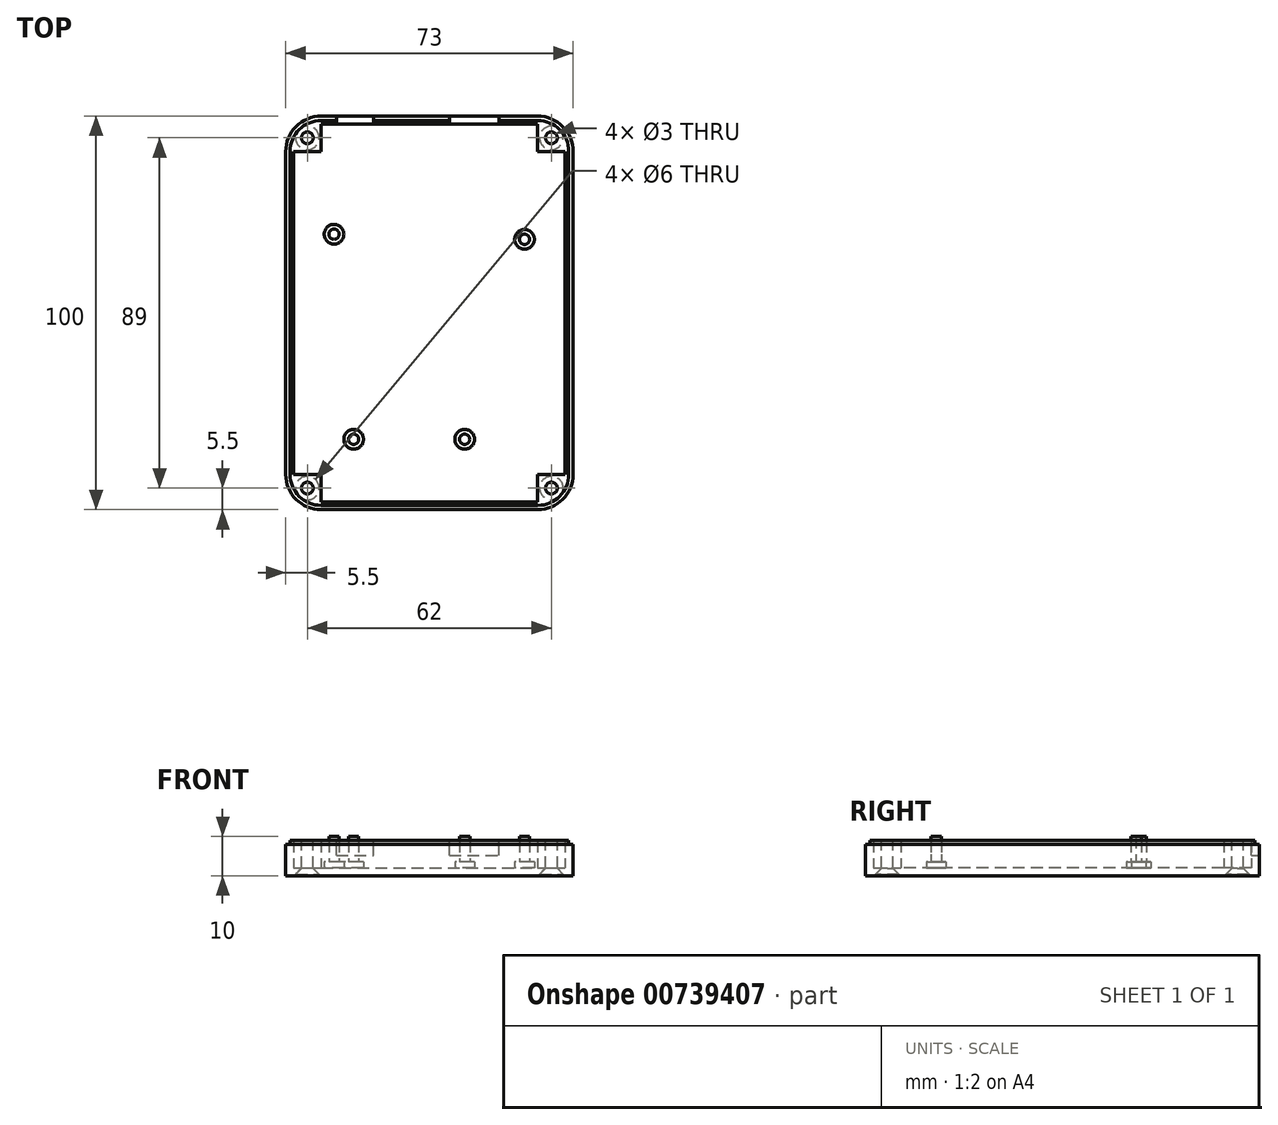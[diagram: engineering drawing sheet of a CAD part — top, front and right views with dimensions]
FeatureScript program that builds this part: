
annotation { "Feature Type Name" : "Feature", "Feature Type Description" : "" }
export const myFeature = defineFeature(function(context is Context, id is Id, definition is map)
    precondition{}
    {
        {
            var Q0;
            Q0=qCreatedBy(makeId("Top.planeOp"),FACE);
            var sketch = newSketch(context, id + "F0", { "sketchPlane" : qUnion([Q0])});
            skLineSegment(sketch, "E0.bottom", {"start": v(-27.5, 63.5) * mm, "end": v(27.5, 63.5) * mm});
            skLineSegment(sketch, "E0.top", {"start": v(-27.5, -36.5) * mm, "end": v(27.5, -36.5) * mm});
            skLineSegment(sketch, "E0.left", {"start": v(-36.5, 54.5) * mm, "end": v(-36.5, -27.5) * mm});
            skLineSegment(sketch, "E0.right", {"start": v(36.5, 54.5) * mm, "end": v(36.5, -27.5) * mm});
            skPoint(sketch, "E1.visualSharp", {"position": v(-36.5, 63.5) * mm});
            skArc(sketch, "E1.filletArc", {"start": v(-27.5, 63.5) * mm, "mid": v(-33.86, 60.86) * mm, "end": v(-36.5, 54.5) * mm});
            skPoint(sketch, "E2.visualSharp", {"position": v(36.5, 63.5) * mm});
            skArc(sketch, "E2.filletArc", {"start": v(36.5, 54.5) * mm, "mid": v(33.86, 60.86) * mm, "end": v(27.5, 63.5) * mm});
            skPoint(sketch, "E3.visualSharp", {"position": v(36.5, -36.5) * mm});
            skArc(sketch, "E3.filletArc", {"start": v(27.5, -36.5) * mm, "mid": v(33.86, -33.86) * mm, "end": v(36.5, -27.5) * mm});
            skPoint(sketch, "E4.visualSharp", {"position": v(-36.5, -36.5) * mm});
            skArc(sketch, "E4.filletArc", {"start": v(-36.5, -27.5) * mm, "mid": v(-33.86, -33.86) * mm, "end": v(-27.5, -36.5) * mm});
            skSolve(sketch);
        }
        {
            var Q0;
            Q0=qSketchRegion(id+"F0",true);
            extrude(context, id + "F1", {"entities" : qUnion([Q0]), "depth" : 2 * mm});
        }
        {
            var Q0;
            Q0=makeQuery(id+"F1.opExtrude","CAP_FACE",FACE,{"disambiguationData":[OSD([sQuery(id+"F0.wireOp",EDGE,"E0.bottom"),sQuery(id+"F0.wireOp",EDGE,"E0.top"),sQuery(id+"F0.wireOp",EDGE,"E0.left"),sQuery(id+"F0.wireOp",EDGE,"E0.right")])],"isStart":false});
            var sketch = newSketch(context, id + "F2", { "sketchPlane" : qUnion([Q0])});
            skCircle(sketch, "E5", {"center": v(-19.24, -18.6) * mm, "radius": 2.5 * mm});
            skCircle(sketch, "E6", {"center": v(8.96, -18.6) * mm, "radius": 2.5 * mm});
            skCircle(sketch, "E7", {"center": v(24.16, 32.2) * mm, "radius": 2.5 * mm});
            skCircle(sketch, "E8", {"center": v(-24.24, 33.5) * mm, "radius": 2.5 * mm});
            skSolve(sketch);
        }
        {
            var Q0;
            Q0=qSketchRegion(id+"F2",true);
            extrude(context, id + "F3", {"entities" : qUnion([Q0]), "operationType" : NewBodyOperationType.ADD, "depth" : 1.5 * mm});
        }
        {
            var Q0;
            Q0=makeQuery(id+"F3.opExtrude","CAP_FACE",FACE,{"disambiguationData":[OSD([sQuery(id+"F2.wireOp",EDGE,"E8")])],"isStart":false});
            var sketch = newSketch(context, id + "F4", { "sketchPlane" : qUnion([Q0])});
            skCircle(sketch, "E9", {"center": v(-19.24, -18.6) * mm, "radius": 1.3 * mm});
            skCircle(sketch, "E10", {"center": v(8.96, -18.6) * mm, "radius": 1.3 * mm});
            skCircle(sketch, "E11", {"center": v(24.16, 32.2) * mm, "radius": 1.3 * mm});
            skCircle(sketch, "E12", {"center": v(-24.24, 33.5) * mm, "radius": 1.3 * mm});
            skSolve(sketch);
        }
        {
            var Q0;
            Q0=qSketchRegion(id+"F4",true);
            extrude(context, id + "F5", {"entities" : qUnion([Q0]), "operationType" : NewBodyOperationType.ADD, "depth" : 1.5 * mm});
        }
        {
            var Q0;
            Q0=makeQuery(id+"F1.opExtrude","CAP_FACE",FACE,{"disambiguationData":[OSD([sQuery(id+"F0.wireOp",EDGE,"E0.bottom"),sQuery(id+"F0.wireOp",EDGE,"E0.top"),sQuery(id+"F0.wireOp",EDGE,"E0.left"),sQuery(id+"F0.wireOp",EDGE,"E0.right"),sQuery(id+"F0.wireOp",EDGE,"E1.filletArc"),sQuery(id+"F0.wireOp",EDGE,"E2.filletArc"),sQuery(id+"F0.wireOp",EDGE,"E3.filletArc"),sQuery(id+"F0.wireOp",EDGE,"E4.filletArc")])],"isStart":false});
            var sketch = newSketch(context, id + "F6", { "sketchPlane" : qUnion([Q0])});
            skLineSegment(sketch, "E13.bottom", {"start": v(-27.5, 63.5) * mm, "end": v(27.5, 63.5) * mm});
            skLineSegment(sketch, "E13.top", {"start": v(-27.5, -36.5) * mm, "end": v(27.5, -36.5) * mm});
            skLineSegment(sketch, "E13.left", {"start": v(-36.5, 54.5) * mm, "end": v(-36.5, -27.5) * mm});
            skLineSegment(sketch, "E13.right", {"start": v(36.5, 54.5) * mm, "end": v(36.5, -27.5) * mm});
            skPoint(sketch, "E14.visualSharp", {"position": v(-36.5, 63.5) * mm});
            skArc(sketch, "E14.filletArc", {"start": v(-27.5, 63.5) * mm, "mid": v(-33.86, 60.86) * mm, "end": v(-36.5, 54.5) * mm});
            skPoint(sketch, "E15.visualSharp", {"position": v(36.5, 63.5) * mm});
            skArc(sketch, "E15.filletArc", {"start": v(36.5, 54.5) * mm, "mid": v(33.86, 60.86) * mm, "end": v(27.5, 63.5) * mm});
            skPoint(sketch, "E16.visualSharp", {"position": v(36.5, -36.5) * mm});
            skArc(sketch, "E16.filletArc", {"start": v(27.5, -36.5) * mm, "mid": v(33.86, -33.86) * mm, "end": v(36.5, -27.5) * mm});
            skPoint(sketch, "E17.visualSharp", {"position": v(-36.5, -36.5) * mm});
            skArc(sketch, "E17.filletArc", {"start": v(-36.5, -27.5) * mm, "mid": v(-33.86, -33.86) * mm, "end": v(-27.5, -36.5) * mm});
            skLineSegment(sketch, "E18", {"start": v(-27.5, 61.5) * mm, "end": v(27.5, 61.5) * mm});
            skLineSegment(sketch, "E19", {"start": v(-34.5, 54.5) * mm, "end": v(-34.5, -27.5) * mm});
            skLineSegment(sketch, "E20", {"start": v(-27.5, -34.5) * mm, "end": v(27.5, -34.5) * mm});
            skLineSegment(sketch, "E21", {"start": v(34.5, 54.5) * mm, "end": v(34.5, -27.5) * mm});
            skLineSegment(sketch, "E22", {"start": v(-34.5, 54.5) * mm, "end": v(-27.5, 54.5) * mm});
            skLineSegment(sketch, "E23", {"start": v(-27.5, 61.5) * mm, "end": v(-27.5, 54.5) * mm});
            skLineSegment(sketch, "E24", {"start": v(27.5, 61.5) * mm, "end": v(27.5, 54.5) * mm});
            skLineSegment(sketch, "E25", {"start": v(27.5, 54.5) * mm, "end": v(34.5, 54.5) * mm});
            skLineSegment(sketch, "E26", {"start": v(-34.5, -27.5) * mm, "end": v(-27.5, -27.5) * mm});
            skLineSegment(sketch, "E27", {"start": v(-27.5, -34.5) * mm, "end": v(-27.5, -27.5) * mm});
            skLineSegment(sketch, "E28", {"start": v(27.5, -34.5) * mm, "end": v(27.5, -27.5) * mm});
            skLineSegment(sketch, "E29", {"start": v(27.5, -27.5) * mm, "end": v(34.5, -27.5) * mm});
            skSolve(sketch);
        }
        {
            var Q0;
            Q0=qSketchRegion(id+"F6",true);
            extrude(context, id + "F7", {"entities" : qUnion([Q0]), "operationType" : NewBodyOperationType.ADD, "depth" : 7 * mm});
        }
        {
            var Q0;
            Q0=makeQuery(id+"F7.opExtrude","CAP_FACE",FACE,{"disambiguationData":[OSD([sQuery(id+"F6.wireOp",EDGE,"E13.bottom"),sQuery(id+"F6.wireOp",EDGE,"E13.top"),sQuery(id+"F6.wireOp",EDGE,"E13.left"),sQuery(id+"F6.wireOp",EDGE,"E13.right"),sQuery(id+"F6.wireOp",EDGE,"E14.filletArc"),sQuery(id+"F6.wireOp",EDGE,"E15.filletArc"),sQuery(id+"F6.wireOp",EDGE,"E16.filletArc"),sQuery(id+"F6.wireOp",EDGE,"E17.filletArc"),sQuery(id+"F6.wireOp",EDGE,"E18"),sQuery(id+"F6.wireOp",EDGE,"E19"),sQuery(id+"F6.wireOp",EDGE,"E20"),sQuery(id+"F6.wireOp",EDGE,"E21"),sQuery(id+"F6.wireOp",EDGE,"E22"),sQuery(id+"F6.wireOp",EDGE,"E23"),sQuery(id+"F6.wireOp",EDGE,"E24"),sQuery(id+"F6.wireOp",EDGE,"E25"),sQuery(id+"F6.wireOp",EDGE,"E26"),sQuery(id+"F6.wireOp",EDGE,"E27"),sQuery(id+"F6.wireOp",EDGE,"E28"),sQuery(id+"F6.wireOp",EDGE,"E29")])],"isStart":false});
            var sketch = newSketch(context, id + "F8", { "sketchPlane" : qUnion([Q0])});
            skCircle(sketch, "E30", {"center": v(-31, 58) * mm, "radius": 1.5 * mm});
            skCircle(sketch, "E31", {"center": v(31, 58) * mm, "radius": 1.5 * mm});
            skCircle(sketch, "E32", {"center": v(-31, -31) * mm, "radius": 1.5 * mm});
            skCircle(sketch, "E33", {"center": v(31, -31) * mm, "radius": 1.5 * mm});
            skSolve(sketch);
        }
        {
            var Q0;
            Q0=qSketchRegion(id+"F8",true);
            extrude(context, id + "F9", {"entities" : qUnion([Q0]), "operationType" : NewBodyOperationType.REMOVE, "oppositeDirection" : true, "depth" : 10 * mm});
        }
        {
            var Q0;
            Q0=makeQuery(id+"F7.opExtrude","CAP_FACE",FACE,{"disambiguationData":[OSD([sQuery(id+"F6.wireOp",EDGE,"E13.bottom"),sQuery(id+"F6.wireOp",EDGE,"E13.top"),sQuery(id+"F6.wireOp",EDGE,"E13.left"),sQuery(id+"F6.wireOp",EDGE,"E13.right"),sQuery(id+"F6.wireOp",EDGE,"E14.filletArc"),sQuery(id+"F6.wireOp",EDGE,"E15.filletArc"),sQuery(id+"F6.wireOp",EDGE,"E16.filletArc"),sQuery(id+"F6.wireOp",EDGE,"E17.filletArc"),sQuery(id+"F6.wireOp",EDGE,"E18"),sQuery(id+"F6.wireOp",EDGE,"E19"),sQuery(id+"F6.wireOp",EDGE,"E20"),sQuery(id+"F6.wireOp",EDGE,"E21"),sQuery(id+"F6.wireOp",EDGE,"E22"),sQuery(id+"F6.wireOp",EDGE,"E23"),sQuery(id+"F6.wireOp",EDGE,"E24"),sQuery(id+"F6.wireOp",EDGE,"E25"),sQuery(id+"F6.wireOp",EDGE,"E26"),sQuery(id+"F6.wireOp",EDGE,"E27"),sQuery(id+"F6.wireOp",EDGE,"E28"),sQuery(id+"F6.wireOp",EDGE,"E29")])],"isStart":false});
            var sketch = newSketch(context, id + "F10", { "sketchPlane" : qUnion([Q0])});
            skLineSegment(sketch, "E34.bottom", {"start": v(17.66, 61.5) * mm, "end": v(5.06, 61.5) * mm});
            skLineSegment(sketch, "E34.top", {"start": v(17.66, 63.5) * mm, "end": v(5.06, 63.5) * mm});
            skLineSegment(sketch, "E34.left", {"start": v(17.66, 61.5) * mm, "end": v(17.66, 63.5) * mm});
            skLineSegment(sketch, "E34.right", {"start": v(5.06, 61.5) * mm, "end": v(5.06, 63.5) * mm});
            skLineSegment(sketch, "E35.bottom", {"start": v(-14.14, 61.5) * mm, "end": v(-23.64, 61.5) * mm});
            skLineSegment(sketch, "E35.top", {"start": v(-14.14, 63.5) * mm, "end": v(-23.64, 63.5) * mm});
            skLineSegment(sketch, "E35.left", {"start": v(-14.14, 61.5) * mm, "end": v(-14.14, 63.5) * mm});
            skLineSegment(sketch, "E35.right", {"start": v(-23.64, 61.5) * mm, "end": v(-23.64, 63.5) * mm});
            skSolve(sketch);
        }
        {
            var Q0;
            Q0=qSketchRegion(id+"F10",true);
            extrude(context, id + "F11", {"entities" : qUnion([Q0]), "operationType" : NewBodyOperationType.REMOVE, "oppositeDirection" : true, "depth" : 3.8 * mm});
        }
        {
            var Q0;
            Q0=makeQuery(id+"F1.opExtrude","CAP_FACE",FACE,{"disambiguationData":[OSD([sQuery(id+"F0.wireOp",EDGE,"E0.bottom"),sQuery(id+"F0.wireOp",EDGE,"E0.top"),sQuery(id+"F0.wireOp",EDGE,"E0.left"),sQuery(id+"F0.wireOp",EDGE,"E0.right"),sQuery(id+"F0.wireOp",EDGE,"E1.filletArc"),sQuery(id+"F0.wireOp",EDGE,"E2.filletArc"),sQuery(id+"F0.wireOp",EDGE,"E3.filletArc"),sQuery(id+"F0.wireOp",EDGE,"E4.filletArc")])],"isStart":true});
            var sketch = newSketch(context, id + "F12", { "sketchPlane" : qUnion([Q0])});
            skCircle(sketch, "E36", {"center": v(31, -58) * mm, "radius": 3 * mm});
            skCircle(sketch, "E37", {"center": v(-31, -58) * mm, "radius": 3 * mm});
            skCircle(sketch, "E38", {"center": v(-31, 31) * mm, "radius": 3 * mm});
            skCircle(sketch, "E39", {"center": v(31, 31) * mm, "radius": 3 * mm});
            skSolve(sketch);
        }
        {
            var Q0;
            Q0=qSketchRegion(id+"F12",true);
            extrude(context, id + "F13", {"entities" : qUnion([Q0]), "operationType" : NewBodyOperationType.REMOVE, "oppositeDirection" : true, "depth" : .4 * mm});
        }
        {
            var Q0;
            Q0=makeQuery(id+"F13.boolean.opBoolean","INTERSECT",EDGE,{"derivedFrom":[makeQuery(id+"F9.boolean.opBoolean","COPY",FACE,{"derivedFrom":makeQuery(id+"F9.opExtrude","SWEPT_FACE",FACE,{"disambiguationData":[OSD([sQuery(id+"F8.wireOp",EDGE,"E31")])]})}),makeQuery(id+"F13.opExtrude","CAP_FACE",FACE,{"disambiguationData":[OSD([sQuery(id+"F12.wireOp",EDGE,"E36")])],"isStart":false})]});
            var Q1;
            Q1=makeQuery(id+"F13.boolean.opBoolean","INTERSECT",EDGE,{"derivedFrom":[makeQuery(id+"F9.boolean.opBoolean","COPY",FACE,{"derivedFrom":makeQuery(id+"F9.opExtrude","SWEPT_FACE",FACE,{"disambiguationData":[OSD([sQuery(id+"F8.wireOp",EDGE,"E30")])]})}),makeQuery(id+"F13.opExtrude","CAP_FACE",FACE,{"disambiguationData":[OSD([sQuery(id+"F12.wireOp",EDGE,"E37")])],"isStart":false})]});
            var Q2;
            Q2=makeQuery(id+"F13.boolean.opBoolean","INTERSECT",EDGE,{"derivedFrom":[makeQuery(id+"F9.boolean.opBoolean","COPY",FACE,{"derivedFrom":makeQuery(id+"F9.opExtrude","SWEPT_FACE",FACE,{"disambiguationData":[OSD([sQuery(id+"F8.wireOp",EDGE,"E33")])]})}),makeQuery(id+"F13.opExtrude","CAP_FACE",FACE,{"disambiguationData":[OSD([sQuery(id+"F12.wireOp",EDGE,"E39")])],"isStart":false})]});
            var Q3;
            Q3=makeQuery(id+"F13.boolean.opBoolean","INTERSECT",EDGE,{"derivedFrom":[makeQuery(id+"F9.boolean.opBoolean","COPY",FACE,{"derivedFrom":makeQuery(id+"F9.opExtrude","SWEPT_FACE",FACE,{"disambiguationData":[OSD([sQuery(id+"F8.wireOp",EDGE,"E32")])]})}),makeQuery(id+"F13.opExtrude","CAP_FACE",FACE,{"disambiguationData":[OSD([sQuery(id+"F12.wireOp",EDGE,"E38")])],"isStart":false})]});
            chamfer(context, id + "F14", {"entities" : qUnion([Q0, Q1, Q2, Q3]), "width" : 1.5 * mm, "tangentPropagation" : true});
        }
        {
            var Q0;
            {var subQ0=sQuery(id+"F6.wireOp",EDGE,"E13.bottom");var subQ1=sQuery(id+"F6.wireOp",EDGE,"E13.top");var subQ2=sQuery(id+"F6.wireOp",EDGE,"E13.left");var subQ3=sQuery(id+"F6.wireOp",EDGE,"E13.right");var subQ4=sQuery(id+"F6.wireOp",EDGE,"E14.filletArc");var subQ5=sQuery(id+"F6.wireOp",EDGE,"E15.filletArc");var subQ6=sQuery(id+"F6.wireOp",EDGE,"E16.filletArc");var subQ7=sQuery(id+"F6.wireOp",EDGE,"E17.filletArc");var subQ8=sQuery(id+"F6.wireOp",EDGE,"E18");var subQ9=sQuery(id+"F6.wireOp",EDGE,"E19");var subQ10=sQuery(id+"F6.wireOp",EDGE,"E20");var subQ11=sQuery(id+"F6.wireOp",EDGE,"E21");var subQ12=sQuery(id+"F6.wireOp",EDGE,"E22");var subQ13=sQuery(id+"F6.wireOp",EDGE,"E23");var subQ14=sQuery(id+"F6.wireOp",EDGE,"E24");var subQ15=sQuery(id+"F6.wireOp",EDGE,"E25");var subQ16=sQuery(id+"F6.wireOp",EDGE,"E26");var subQ17=sQuery(id+"F6.wireOp",EDGE,"E27");var subQ18=sQuery(id+"F6.wireOp",EDGE,"E28");var subQ19=sQuery(id+"F6.wireOp",EDGE,"E29");Q0=makeQuery(id+"F11.boolean.opBoolean","SPLIT",FACE,{"disambiguationData":[TD([makeQuery(id+"F1.opExtrude","SWEPT_FACE",FACE,{"disambiguationData":[OSD([sQuery(id+"F0.wireOp",EDGE,"E0.top")])]})])],"derivedFrom":makeQuery(id+"F7.opExtrude","CAP_FACE",FACE,{"disambiguationData":[OSD([subQ0,subQ1,subQ2,subQ3,subQ4,subQ5,subQ6,subQ7,subQ8,subQ9,subQ10,subQ11,subQ12,subQ13,subQ14,subQ15,subQ16,subQ17,subQ18,subQ19])],"isStart":false})});}
            var sketch = newSketch(context, id + "F15", { "sketchPlane" : qUnion([Q0])});
            skLineSegment(sketch, "E40.0", {"start": v(-27.5, 63.5) * mm, "end": v(-23.64, 63.5) * mm});
            skArc(sketch, "E40.1", {"start": v(-27.5, 63.5) * mm, "mid": v(-33.86, 60.86) * mm, "end": v(-36.5, 54.5) * mm});
            skLineSegment(sketch, "E40.2", {"start": v(-36.5, 54.5) * mm, "end": v(-36.5, -27.5) * mm});
            skArc(sketch, "E40.3", {"start": v(-36.5, -27.5) * mm, "mid": v(-33.86, -33.86) * mm, "end": v(-27.5, -36.5) * mm});
            skLineSegment(sketch, "E40.4", {"start": v(-27.5, -36.5) * mm, "end": v(27.5, -36.5) * mm});
            skArc(sketch, "E40.5", {"start": v(27.5, -36.5) * mm, "mid": v(33.86, -33.86) * mm, "end": v(36.5, -27.5) * mm});
            skLineSegment(sketch, "E40.6", {"start": v(36.5, 54.5) * mm, "end": v(36.5, -27.5) * mm});
            skArc(sketch, "E40.7", {"start": v(36.5, 54.5) * mm, "mid": v(33.86, 60.86) * mm, "end": v(27.5, 63.5) * mm});
            skLineSegment(sketch, "E40.8", {"start": v(17.66, 63.5) * mm, "end": v(27.5, 63.5) * mm});
            skLineSegment(sketch, "E40.9", {"start": v(-14.14, 63.5) * mm, "end": v(5.06, 63.5) * mm});
            skLineSegment(sketch, "E41.top", {"start": v(-14.14, 62.4) * mm, "end": v(5.06, 62.4) * mm});
            skLineSegment(sketch, "E41.left", {"start": v(-14.14, 63.5) * mm, "end": v(-14.14, 62.4) * mm});
            skLineSegment(sketch, "E41.right", {"start": v(5.06, 63.5) * mm, "end": v(5.06, 62.4) * mm});
            skLineSegment(sketch, "E42", {"start": v(-35.4, 54.5) * mm, "end": v(-35.4, -27.5) * mm});
            skLineSegment(sketch, "E43", {"start": v(35.4, 54.5) * mm, "end": v(35.4, -27.5) * mm});
            skLineSegment(sketch, "E44", {"start": v(-27.5, -35.4) * mm, "end": v(27.5, -35.4) * mm});
            skLineSegment(sketch, "E45", {"start": v(-27.5, 62.4) * mm, "end": v(-23.64, 62.4) * mm});
            skLineSegment(sketch, "E46", {"start": v(-23.64, 62.4) * mm, "end": v(-23.64, 63.5) * mm});
            skArc(sketch, "E47", {"start": v(-27.5, 62.4) * mm, "mid": v(-33.09, 60.09) * mm, "end": v(-35.4, 54.5) * mm});
            skLineSegment(sketch, "E48", {"start": v(27.5, 62.4) * mm, "end": v(17.66, 62.4) * mm});
            skLineSegment(sketch, "E49", {"start": v(17.66, 63.5) * mm, "end": v(17.66, 62.4) * mm});
            skArc(sketch, "E50", {"start": v(35.4, 54.5) * mm, "mid": v(33.09, 60.09) * mm, "end": v(27.5, 62.4) * mm});
            skArc(sketch, "E51", {"start": v(27.5, -35.4) * mm, "mid": v(33.09, -33.09) * mm, "end": v(35.4, -27.5) * mm});
            skArc(sketch, "E52", {"start": v(-35.4, -27.5) * mm, "mid": v(-33.09, -33.09) * mm, "end": v(-27.5, -35.4) * mm});
            skSolve(sketch);
        }
        {
            var Q0;
            Q0=qSketchRegion(id+"F15",true);
            extrude(context, id + "F16", {"entities" : qUnion([Q0]), "operationType" : NewBodyOperationType.REMOVE, "oppositeDirection" : true, "depth" : 1 * mm});
        }
        {
            var Q0;
            Q0=makeQuery(id+"F5.opExtrude","CAP_FACE",FACE,{"disambiguationData":[OSD([sQuery(id+"F4.wireOp",EDGE,"E9")])],"isStart":false});
            var Q1;
            Q1=makeQuery(id+"F5.opExtrude","CAP_FACE",FACE,{"disambiguationData":[OSD([sQuery(id+"F4.wireOp",EDGE,"E10")])],"isStart":false});
            var Q2;
            Q2=makeQuery(id+"F5.opExtrude","CAP_FACE",FACE,{"disambiguationData":[OSD([sQuery(id+"F4.wireOp",EDGE,"E11")])],"isStart":false});
            var Q3;
            Q3=makeQuery(id+"F5.opExtrude","CAP_FACE",FACE,{"disambiguationData":[OSD([sQuery(id+"F4.wireOp",EDGE,"E12")])],"isStart":false});
            extrude(context, id + "F17", {"entities" : qUnion([Q0, Q1, Q2, Q3]), "operationType" : NewBodyOperationType.ADD, "depth" : 5 * mm, "offsetDistance" : 25 * mm});
        }
    });
